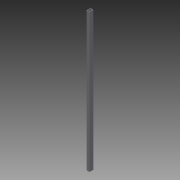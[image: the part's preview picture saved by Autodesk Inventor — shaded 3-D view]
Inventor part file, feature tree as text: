
AUTODESK INVENTOR PART (.ipt)
format: ipt  version: 2013 (Build 170138000, 138)  size: 78,336 bytes
history: native  units: in
note: dims shown in document units (in); Inventor stores cm internally (conversion verified against a paired STEP export)
features: other x2, extrude x1, sketch x1
ambient origin geometry x8: Origin, YZ Plane, XZ Plane, XY Plane, X Axis, Y Axis, Z Axis, Center Point
bodies: Solid1 (feature_tree)
feature tree (4):
  other  "Table"
  other  "squareTube1.5x2-01"
  extrude  "Extrusion1"  Depth=2.0in
  sketch  "Sketch1"  dims[d0=1.5in d1=2.0in d2=0.125in d4=0.0in]
